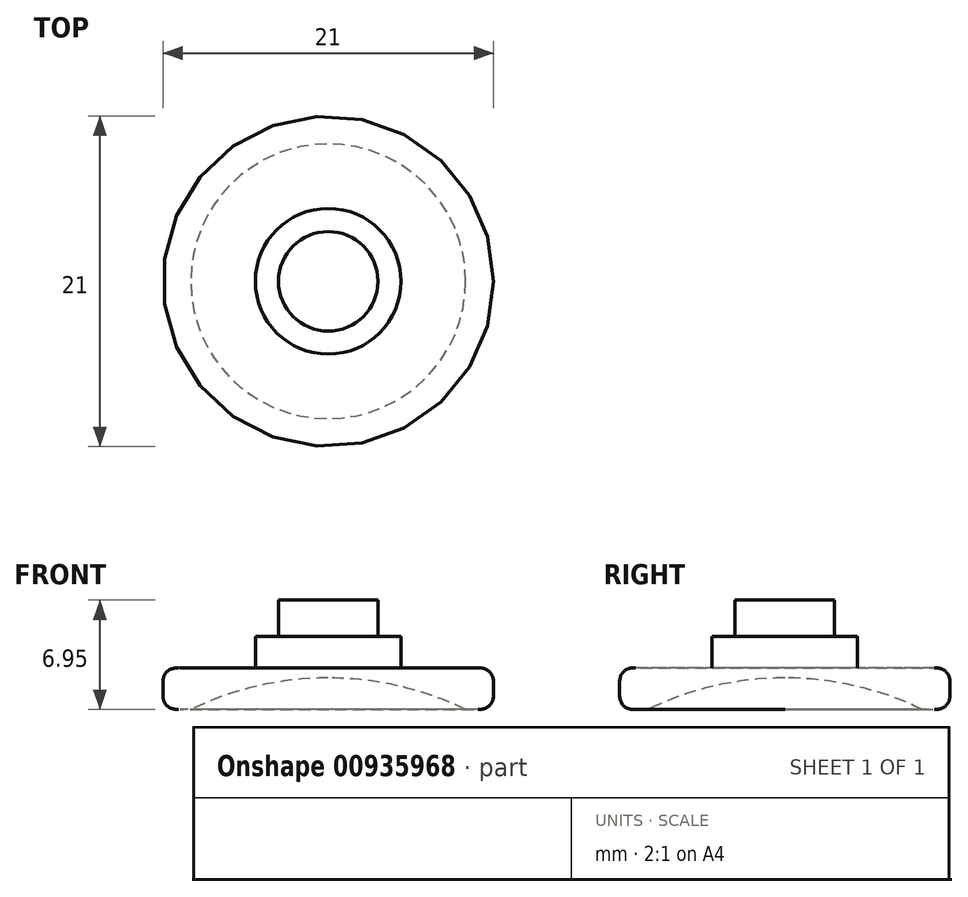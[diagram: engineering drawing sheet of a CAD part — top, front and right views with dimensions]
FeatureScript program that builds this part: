
annotation { "Feature Type Name" : "Feature", "Feature Type Description" : "" }
export const myFeature = defineFeature(function(context is Context, id is Id, definition is map)
    precondition{}
    {
        {
            var Q0;
            Q0=qCreatedBy(makeId("Top.planeOp"),FACE);
            var sketch = newSketch(context, id + "F0", { "sketchPlane" : qUnion([Q0])});
            skCircle(sketch, "E0", {"center": v(0, 0) * mm, "radius": 10.5 * mm});
            skSolve(sketch);
        }
        {
            var Q0;
            Q0=makeQuery(id+"F0.imprint","IMPRINT",FACE,{"disambiguationData":[TD([[makeQuery(id+"F0.imprint","IMPRINT",EDGE,{"derivedFrom":sQuery(id+"F0.wireOp",EDGE,"E0")}),1.0]])]});
            extrude(context, id + "F1", {"entities" : qUnion([Q0]), "depth" : 2.65 * mm, "offsetDistance" : 25 * mm});
        }
        {
            var Q0;
            Q0=makeQuery(id+"F1.opExtrude","CAP_FACE",FACE,{"disambiguationData":[OSD([sQuery(id+"F0.wireOp",EDGE,"E0")])],"isStart":false});
            var sketch = newSketch(context, id + "F2", { "sketchPlane" : qUnion([Q0])});
            skCircle(sketch, "E1", {"center": v(0, 0) * mm, "radius": 4.62 * mm});
            skSolve(sketch);
        }
        {
            var Q0;
            Q0 = qSketchRegion(id + "F2", true);
            extrude(context, id + "F3", {"entities" : qUnion([Q0]), "operationType" : NewBodyOperationType.ADD, "depth" : 2 * mm, "offsetDistance" : 25 * mm});
        }
        {
            var Q0;
            Q0=makeQuery(id+"F3.opExtrude","CAP_FACE",FACE,{"disambiguationData":[OSD([sQuery(id+"F2.wireOp",EDGE,"E1")])],"isStart":false});
            var sketch = newSketch(context, id + "F4", { "sketchPlane" : qUnion([Q0])});
            skCircle(sketch, "E2", {"center": v(0, 0) * mm, "radius": 3.16 * mm});
            skSolve(sketch);
        }
        {
            var Q0;
            Q0=makeQuery(id+"F4.imprint","IMPRINT",FACE,{"disambiguationData":[TD([[makeQuery(id+"F4.imprint","IMPRINT",EDGE,{"derivedFrom":sQuery(id+"F4.wireOp",EDGE,"E2")}),1.0]])]});
            var Q1;
            Q1=sQuery(id+"F4.wireOp",EDGE,"E2");
            extrude(context, id + "F5", {"entities" : qUnion([Q0]), "operationType" : NewBodyOperationType.ADD, "surfaceEntities" : qUnion([Q1]), "depth" : 2.3 * mm, "offsetDistance" : 25 * mm});
        }
        {
            var Q0;
            Q0=qCreatedBy(makeId("Front.planeOp"),FACE);
            var sketch = newSketch(context, id + "F6", { "sketchPlane" : qUnion([Q0])});
            skLineSegment(sketch, "E3", {"start": v(0, 0) * mm, "end": v(0, 2) * mm});
            skArc(sketch, "E4", {"start": v(8.73, 0) * mm, "mid": v(4.48, 1.5) * mm, "end": v(0, 2) * mm});
            skLineSegment(sketch, "E5", {"start": v(0, 0) * mm, "end": v(8.73, 0) * mm});
            skSolve(sketch);
        }
        {
            var Q0;
            Q0 = qSketchRegion(id + "F6", true);
            var Q1;
            Q1=sQuery(id+"F6.wireOp",EDGE,"E3");
            revolve(context, id + "F7", {"operationType" : NewBodyOperationType.REMOVE, "surfaceOperationType" : NewSurfaceOperationType.NEW, "entities" : qUnion([Q0]), "axis" : qUnion([Q1]), "revolveType" : RevolveType.FULL, "oppositeDirection" : true});
        }
        {
            var Q0;
            Q0=makeQuery(id+"F1.opExtrude","CAP_EDGE",EDGE,{"disambiguationData":[OSD([sQuery(id+"F0.wireOp",EDGE,"E0")])],"isStart":true});
            fillet(context, id + "F8", {"entities" : qUnion([Q0]), "radius" : 1 * mm, "rho" : .5, "crossSection" : FilletCrossSection.CONIC, "allowEdgeOverflow" : false});
        }
        {
            var Q0;
            Q0=makeQuery(id+"F1.opExtrude","CAP_EDGE",EDGE,{"disambiguationData":[OSD([sQuery(id+"F0.wireOp",EDGE,"E0")])],"isStart":false});
            fillet(context, id + "F9", {"entities" : qUnion([Q0]), "radius" : 1 * mm, "rho" : 0.5, "crossSection" : FilletCrossSection.CONIC, "allowEdgeOverflow" : false});
        }
    });
